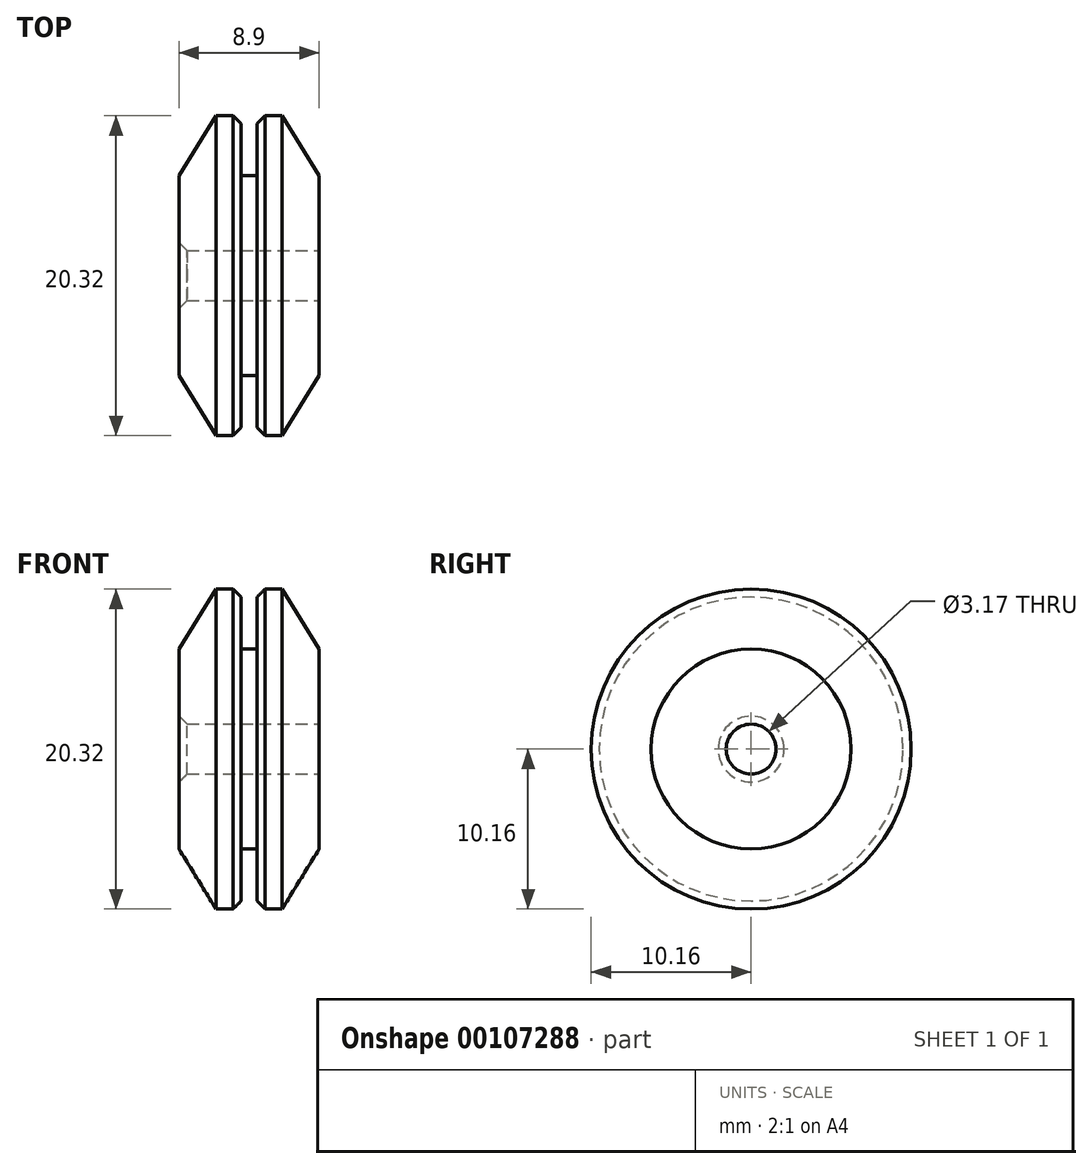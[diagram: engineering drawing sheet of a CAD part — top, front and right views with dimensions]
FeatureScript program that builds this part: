
annotation { "Feature Type Name" : "Feature", "Feature Type Description" : "" }
export const myFeature = defineFeature(function(context is Context, id is Id, definition is map)
    precondition{}
    {
        {
            var Q0;
            Q0=qCreatedBy(makeId("Front.planeOp"),FACE);
            var sketch = newSketch(context, id + "F0", { "sketchPlane" : qUnion([Q0])});
            skLineSegment(sketch, "E0", {"start": v(0, 6.35) * mm, "end": v(-0.5, 6.35) * mm});
            skLineSegment(sketch, "E1", {"start": v(-0.5, 6.35) * mm, "end": v(-0.5, 10.16) * mm});
            skLineSegment(sketch, "E2", {"start": v(0.5, 10.16) * mm, "end": v(0.5, 6.35) * mm});
            skLineSegment(sketch, "E3", {"start": v(0.5, 6.35) * mm, "end": v(0, 6.35) * mm});
            skLineSegment(sketch, "E4", {"start": v(4.44, 6.35) * mm, "end": v(4.44, 0) * mm});
            skLineSegment(sketch, "E5", {"start": v(4.44, 0) * mm, "end": v(-4.44, 0) * mm});
            skLineSegment(sketch, "E6", {"start": v(-4.44, 0) * mm, "end": v(-4.44, 6.35) * mm});
            skLineSegment(sketch, "E7", {"start": v(0.5, 10.16) * mm, "end": v(2.1, 10.16) * mm});
            skLineSegment(sketch, "E8", {"start": v(2.1, 10.16) * mm, "end": v(4.44, 6.35) * mm});
            skLineSegment(sketch, "E9", {"start": v(-0.5, 10.16) * mm, "end": v(-2.1, 10.16) * mm});
            skLineSegment(sketch, "E10", {"start": v(-2.1, 10.16) * mm, "end": v(-4.45, 6.35) * mm});
            skSolve(sketch);
        }
        {
            var Q0;
            Q0=qSketchRegion(id+"F0",true);
            var Q1;
            Q1=sQuery(id+"F0.wireOp",EDGE,"E5");
            revolve(context, id + "F1", {"entities" : qUnion([Q0]), "axis" : qUnion([Q1]), "revolveType" : RevolveType.FULL});
        }
        {
            var Q0;
            Q0=makeQuery(id+"F1.opRevolve","SWEPT_FACE",FACE,{"disambiguationData":[OSD([sQuery(id+"F0.wireOp",EDGE,"E4")])]});
            var sketch = newSketch(context, id + "F2", { "sketchPlane" : qUnion([Q0])});
            skCircle(sketch, "E11", {"center": v(0, 0) * mm, "radius": 1.59 * mm});
            skSolve(sketch);
        }
        {
            var Q0;
            Q0=makeQuery(id+"F2.imprint","IMPRINT",FACE,{"disambiguationData":[TD([[makeQuery(id+"F2.imprint","IMPRINT",EDGE,{"derivedFrom":sQuery(id+"F2.wireOp",EDGE,"E11")}),1.0]])]});
            extrude(context, id + "F3", {"entities" : qUnion([Q0]), "operationType" : NewBodyOperationType.REMOVE, "endBound" : BoundingType.THROUGH_ALL, "oppositeDirection" : true, "depth" : 25.4 * mm});
        }
        {
            var Q0;
            Q0=makeQuery(id+"F3.boolean.opBoolean","INTERSECT",EDGE,{"derivedFrom":[makeQuery(id+"F1.opRevolve","SWEPT_FACE",FACE,{"disambiguationData":[OSD([sQuery(id+"F0.wireOp",EDGE,"E6")])]}),makeQuery(id+"F3.opExtrude","SWEPT_FACE",FACE,{"disambiguationData":[OSD([sQuery(id+"F2.wireOp",EDGE,"E11")])]})]});
            var Q1;
            Q1=makeQuery(id+"F3.boolean.opBoolean","COPY",EDGE,{"derivedFrom":makeQuery(id+"F3.opExtrude","CAP_EDGE",EDGE,{"disambiguationData":[OSD([sQuery(id+"F2.wireOp",EDGE,"E11")])],"isStart":true})});
            chamfer(context, id + "F4", {"entities" : qUnion([Q0, Q1]), "width" : 0.5 * mm, "tangentPropagation" : true});
        }
        {
            var Q0;
            Q0=makeQuery(id+"F1.opRevolve","SWEPT_EDGE",EDGE,{"disambiguationData":[OSD([sQuery(id+"F0.wireOp",EDGE,"E1"),sQuery(id+"F0.wireOp",EDGE,"E9")])]});
            var Q1;
            Q1=makeQuery(id+"F1.opRevolve","SWEPT_EDGE",EDGE,{"disambiguationData":[OSD([sQuery(id+"F0.wireOp",EDGE,"E2"),sQuery(id+"F0.wireOp",EDGE,"E7")])]});
            chamfer(context, id + "F5", {"entities" : qUnion([Q0, Q1]), "width" : 0.5 * mm, "tangentPropagation" : true});
        }
    });
